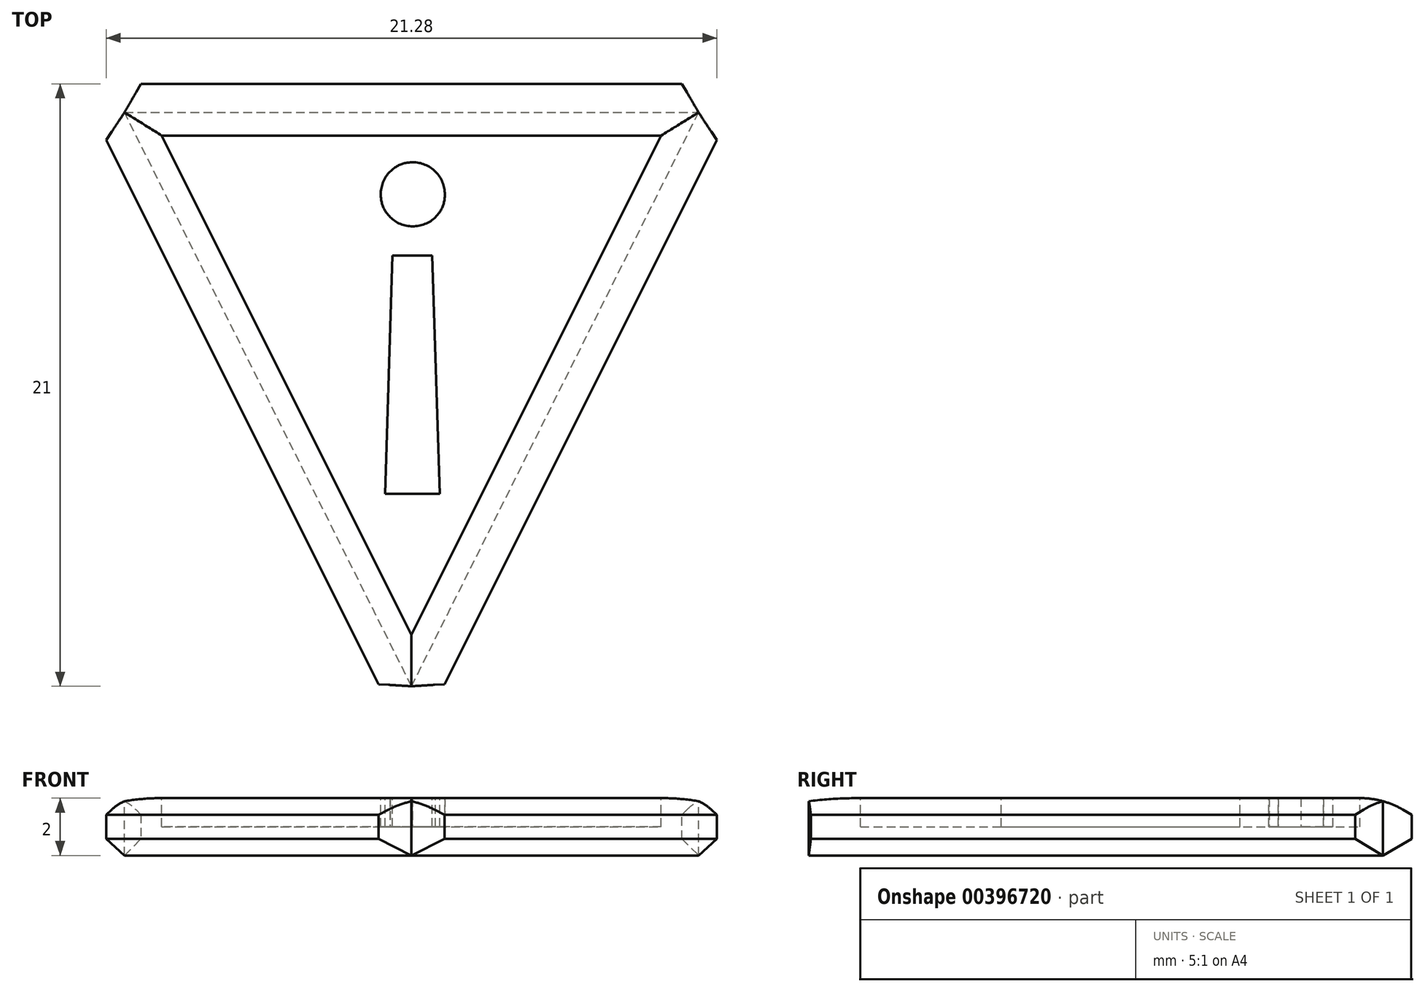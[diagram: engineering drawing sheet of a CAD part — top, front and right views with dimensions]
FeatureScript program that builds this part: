
annotation { "Feature Type Name" : "Feature", "Feature Type Description" : "" }
export const myFeature = defineFeature(function(context is Context, id is Id, definition is map)
    precondition{}
    {
        {
            var Q0;
            Q0=qCreatedBy(makeId("Top.planeOp"),FACE);
            var sketch = newSketch(context, id + "F0", { "sketchPlane" : qUnion([Q0])});
            skLineSegment(sketch, "E0", {"start": v(-10, 0) * mm, "end": v(10, 0) * mm});
            skLineSegment(sketch, "E1", {"start": v(0, 0) * mm, "end": v(0, 20) * mm});
            skLineSegment(sketch, "E2", {"start": v(0, 20) * mm, "end": v(10, 0) * mm});
            skLineSegment(sketch, "E3", {"start": v(0, 20) * mm, "end": v(-10, 0) * mm});
            skSolve(sketch);
        }
        {
            var Q0;
            {var subQ2=sQuery(id+"F0.wireOp",EDGE,"E1");Q0=makeQuery(id+"F0.imprint","IMPRINT",FACE,{"disambiguationData":[TD([[makeQuery(id+"F0.imprint","IMPRINT",EDGE,{"derivedFrom":subQ2}),-1.0]])]});}
            var Q1;
            {var subQ2=sQuery(id+"F0.wireOp",EDGE,"E1");Q1=makeQuery(id+"F0.imprint","IMPRINT",FACE,{"disambiguationData":[TD([[makeQuery(id+"F0.imprint","IMPRINT",EDGE,{"derivedFrom":subQ2}),1.0]])]});}
            extrude(context, id + "F1", {"entities" : qUnion([Q0, Q1]), "depth" : 2 * mm});
        }
        {
            var Q0;
            Q0=makeQuery(id+"F1.opExtrude","SWEPT_FACE",FACE,{"disambiguationData":[OSD([sQuery(id+"F0.wireOp",EDGE,"E3")])]});
            extrude(context, id + "F2", {"entities" : qUnion([Q0]), "operationType" : NewBodyOperationType.ADD, "depth" : 1 * mm, "hasDraft" : true, "draftAngle" : 30 * degree, "draftPullDirection" : true});
        }
        {
            var Q0;
            Q0=makeQuery(id+"F1.opExtrude","SWEPT_FACE",FACE,{"disambiguationData":[OSD([sQuery(id+"F0.wireOp",EDGE,"E2")])]});
            extrude(context, id + "F3", {"entities" : qUnion([Q0]), "operationType" : NewBodyOperationType.ADD, "depth" : 1 * mm, "hasDraft" : true, "draftAngle" : 30 * degree, "draftPullDirection" : true});
        }
        {
            var Q0;
            Q0=makeQuery(id+"F1.opExtrude","SWEPT_FACE",FACE,{"disambiguationData":[OSD([sQuery(id+"F0.wireOp",EDGE,"E0")])]});
            extrude(context, id + "F4", {"entities" : qUnion([Q0]), "operationType" : NewBodyOperationType.ADD, "depth" : 1 * mm, "hasDraft" : true, "draftAngle" : 30 * degree, "draftPullDirection" : true});
        }
        {
            var Q0;
            Q0=makeQuery(id+"F1.opExtrude","CAP_FACE",FACE,{"disambiguationData":[OSD([sQuery(id+"F0.wireOp",EDGE,"E0"),sQuery(id+"F0.wireOp",EDGE,"E2"),sQuery(id+"F0.wireOp",EDGE,"E3")])],"isStart":true});
            fillet(context, id + "F5", {"entities" : qUnion([Q0]), "radius" : 3 * mm, "tangentPropagation" : true, "allowEdgeOverflow" : false});
        }
        {
            var Q0;
            Q0=makeQuery(id+"F1.opExtrude","CAP_FACE",FACE,{"disambiguationData":[OSD([sQuery(id+"F0.wireOp",EDGE,"E0"),sQuery(id+"F0.wireOp",EDGE,"E2"),sQuery(id+"F0.wireOp",EDGE,"E3")])],"isStart":true});
            extrude(context, id + "F6", {"entities" : qUnion([Q0]), "operationType" : NewBodyOperationType.REMOVE, "oppositeDirection" : true, "depth" : 1 * mm});
        }
        {
            var Q0;
            Q0=qCreatedBy(makeId("Top.planeOp"),FACE);
            var sketch = newSketch(context, id + "F7", { "sketchPlane" : qUnion([Q0])});
            skText(sketch, "E4", { "text": "!", "fontName": "AllertaStencil-Regular.ttf"});
            const initialGuessF7  = {"E4": [-0.00224, 0.0018, 1, 0, 0.0115]};
            skSetInitialGuess(sketch, initialGuessF7);
            skSolve(sketch);
        }
        {
            var Q0;
            Q0=makeQuery(id+"F7.imprint","IMPRINT",FACE,{"disambiguationData":[TD([[makeQuery(id+"F7.imprint","IMPRINT",EDGE,{"derivedFrom":sQuery(id+"F7.wireOp",EDGE,"E4.sketch_text.stroke-0")}),-1.0]])]});
            var Q1;
            Q1=makeQuery(id+"F7.imprint","IMPRINT",FACE,{"disambiguationData":[TD([[makeQuery(id+"F7.imprint","IMPRINT",EDGE,{"derivedFrom":sQuery(id+"F7.wireOp",EDGE,"E4.sketch_text.stroke-4")}),-1.0]])]});
            extrude(context, id + "F8", {"entities" : qUnion([Q0, Q1]), "operationType" : NewBodyOperationType.ADD, "depth" : 1.1 * mm});
        }
        {
            var Q0;
            Q0=makeQuery(id+"F1.opExtrude","SWEPT_BODY",BODY,{"disambiguationData":[OSD([sQuery(id+"F0.wireOp",EDGE,"E0"),sQuery(id+"F0.wireOp",EDGE,"E2"),sQuery(id+"F0.wireOp",EDGE,"E3")])]});
            var Q1;
            {var subQ0=sQuery(id+"F0.wireOp",EDGE,"E0");var subQ1=makeQuery(id+"F1.opExtrude","CAP_EDGE",EDGE,{"disambiguationData":[OSD([subQ0])],"isStart":false});Q1=makeQuery(id+"F4.boolean.opBoolean","MERGE",EDGE,{"derivedFrom":[subQ1,makeQuery(id+"F4.opExtrude","CAP_EDGE",EDGE,{"disambiguationData":[OSD([subQ0]),TDD([subQ1])],"isStart":true})]});}
            transform(context, id + "F9", {"entities" : qUnion([Q0]), "transformType" : TransformType.ROTATION, "transformAxis" : qUnion([Q1]), "angle" : 180 * degree, "makeCopy" : false});
        }
    });
